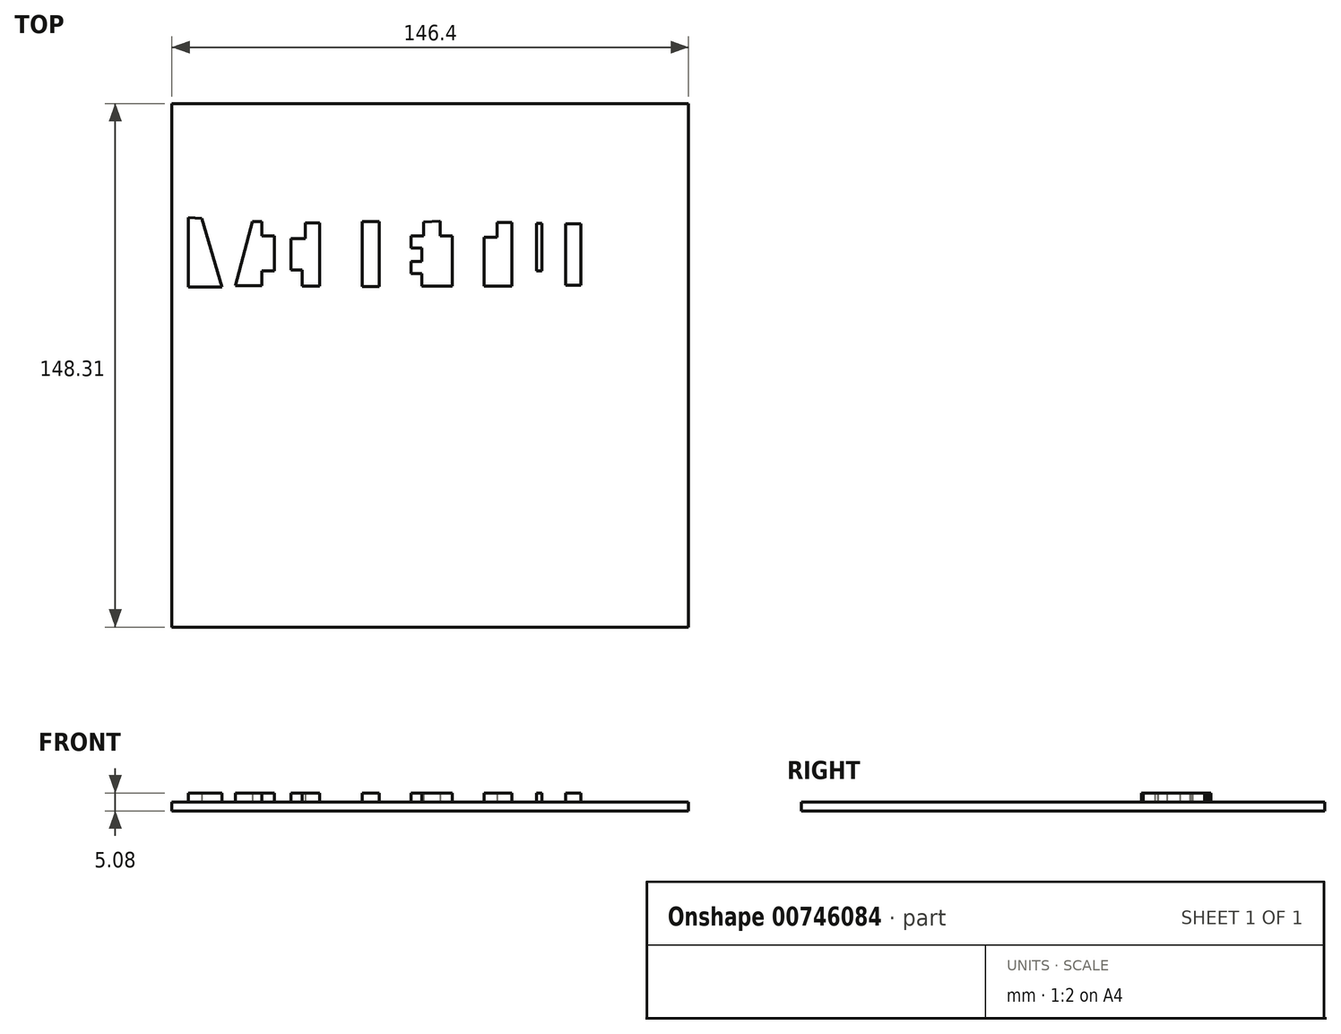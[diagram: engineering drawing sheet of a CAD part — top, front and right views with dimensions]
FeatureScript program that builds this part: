
annotation { "Feature Type Name" : "Feature", "Feature Type Description" : "" }
export const myFeature = defineFeature(function(context is Context, id is Id, definition is map)
    precondition{}
    {
        {
            var Q0;
            Q0=qCreatedBy(makeId("Top.planeOp"),FACE);
            var sketch = newSketch(context, id + "F0", { "sketchPlane" : qUnion([Q0])});
            skLineSegment(sketch, "E0.bottom", {"start": v(-73.41, 74.3) * mm, "end": v(72.99, 74.3) * mm});
            skLineSegment(sketch, "E0.top", {"start": v(-73.41, -74.02) * mm, "end": v(72.99, -74.02) * mm});
            skLineSegment(sketch, "E0.left", {"start": v(-73.41, 74.3) * mm, "end": v(-73.41, -74.02) * mm});
            skLineSegment(sketch, "E0.right", {"start": v(72.99, 74.3) * mm, "end": v(72.99, -74.02) * mm});
            skSolve(sketch);
        }
        {
            var Q0;
            Q0=makeQuery(id+"F0.imprint","IMPRINT",FACE,{"disambiguationData":[TD([[makeQuery(id+"F0.imprint","IMPRINT",EDGE,{"derivedFrom":sQuery(id+"F0.wireOp",EDGE,"E0.bottom")}),-1.0]])]});
            extrude(context, id + "F1", {"entities" : qUnion([Q0]), "depth" : 2.54 * mm, "offsetDistance" : 25.4 * mm});
        }
        {
            var Q0;
            Q0=qCreatedBy(makeId("Top.planeOp"),FACE);
            cPlane(context, id + "F2", {"entities" : qUnion([Q0]), "cplaneType" : CPlaneType.OFFSET, "offset" : 2.54 * mm, "width" : 152.4 * mm, "height" : 152.4 * mm});
        }
        {
            var Q0;
            Q0=qCreatedBy(id+"F2.planeOp",FACE);
            var sketch = newSketch(context, id + "F3", { "sketchPlane" : qUnion([Q0])});
            skLineSegment(sketch, "E1", {"start": v(-68.7, 42.02) * mm, "end": v(-68.7, 22.38) * mm});
            skLineSegment(sketch, "E2", {"start": v(-68.7, 22.38) * mm, "end": v(-59.25, 22.38) * mm});
            skLineSegment(sketch, "E3", {"start": v(-59.25, 22.38) * mm, "end": v(-64.96, 41.77) * mm});
            skLineSegment(sketch, "E4", {"start": v(-64.96, 41.77) * mm, "end": v(-68.7, 42.02) * mm});
            skSolve(sketch);
        }
        {
            var Q0;
            Q0=makeQuery(id+"F3.imprint","IMPRINT",FACE,{"disambiguationData":[TD([[makeQuery(id+"F3.imprint","IMPRINT",EDGE,{"derivedFrom":sQuery(id+"F3.wireOp",EDGE,"E1")}),1.0]])]});
            extrude(context, id + "F4", {"entities" : qUnion([Q0]), "operationType" : NewBodyOperationType.ADD, "depth" : 2.54 * mm, "offsetDistance" : 25.4 * mm});
        }
        {
            var Q0;
            Q0=qCreatedBy(id+"F2.planeOp",FACE);
            var sketch = newSketch(context, id + "F5", { "sketchPlane" : qUnion([Q0])});
            skLineSegment(sketch, "E5", {"start": v(-55.37, 22.74) * mm, "end": v(-47.92, 22.74) * mm});
            skLineSegment(sketch, "E6", {"start": v(-47.92, 22.74) * mm, "end": v(-47.92, 26.92) * mm});
            skLineSegment(sketch, "E7", {"start": v(-47.92, 26.92) * mm, "end": v(-44.4, 26.92) * mm});
            skLineSegment(sketch, "E8", {"start": v(-44.4, 26.92) * mm, "end": v(-44.4, 36.84) * mm});
            skLineSegment(sketch, "E9", {"start": v(-44.4, 36.84) * mm, "end": v(-47.92, 36.84) * mm});
            skLineSegment(sketch, "E10", {"start": v(-47.92, 36.84) * mm, "end": v(-47.92, 40.86) * mm});
            skLineSegment(sketch, "E11", {"start": v(-47.92, 40.86) * mm, "end": v(-50.53, 40.86) * mm});
            skLineSegment(sketch, "E12", {"start": v(-50.53, 40.86) * mm, "end": v(-55.37, 22.74) * mm});
            skSolve(sketch);
        }
        {
            var Q0;
            Q0=makeQuery(id+"F5.imprint","IMPRINT",FACE,{"disambiguationData":[TD([[makeQuery(id+"F5.imprint","IMPRINT",EDGE,{"derivedFrom":sQuery(id+"F5.wireOp",EDGE,"E5")}),1.0]])]});
            extrude(context, id + "F6", {"entities" : qUnion([Q0]), "operationType" : NewBodyOperationType.ADD, "depth" : 2.54 * mm, "offsetDistance" : 25.4 * mm});
        }
        {
            var Q0;
            Q0=qCreatedBy(id+"F2.planeOp",FACE);
            var sketch = newSketch(context, id + "F7", { "sketchPlane" : qUnion([Q0])});
            skLineSegment(sketch, "E13", {"start": v(-39.62, 36.06) * mm, "end": v(-39.62, 27.12) * mm});
            skLineSegment(sketch, "E14", {"start": v(-39.62, 27.12) * mm, "end": v(-36.45, 27.12) * mm});
            skLineSegment(sketch, "E15", {"start": v(-36.45, 27.12) * mm, "end": v(-36.45, 22.62) * mm});
            skLineSegment(sketch, "E16", {"start": v(-36.45, 22.62) * mm, "end": v(-31.5, 22.62) * mm});
            skLineSegment(sketch, "E17", {"start": v(-31.5, 22.62) * mm, "end": v(-31.5, 40.5) * mm});
            skLineSegment(sketch, "E18", {"start": v(-31.5, 40.5) * mm, "end": v(-35.62, 40.5) * mm});
            skLineSegment(sketch, "E19", {"start": v(-35.62, 40.5) * mm, "end": v(-35.62, 36.04) * mm});
            skLineSegment(sketch, "E20", {"start": v(-35.62, 36.04) * mm, "end": v(-39.62, 36.06) * mm});
            skSolve(sketch);
        }
        {
            var Q0;
            Q0=makeQuery(id+"F7.imprint","IMPRINT",FACE,{"disambiguationData":[TD([[makeQuery(id+"F7.imprint","IMPRINT",EDGE,{"derivedFrom":sQuery(id+"F7.wireOp",EDGE,"E13")}),1.0]])]});
            extrude(context, id + "F8", {"entities" : qUnion([Q0]), "operationType" : NewBodyOperationType.ADD, "depth" : 2.54 * mm, "offsetDistance" : 25.4 * mm});
        }
        {
            var Q0;
            Q0=qCreatedBy(id+"F2.planeOp",FACE);
            var sketch = newSketch(context, id + "F9", { "sketchPlane" : qUnion([Q0])});
            skLineSegment(sketch, "E21.bottom", {"start": v(-19.46, 40.9) * mm, "end": v(-14.6, 40.9) * mm});
            skLineSegment(sketch, "E21.top", {"start": v(-19.46, 22.48) * mm, "end": v(-14.6, 22.48) * mm});
            skLineSegment(sketch, "E21.left", {"start": v(-19.46, 40.9) * mm, "end": v(-19.46, 22.48) * mm});
            skLineSegment(sketch, "E21.right", {"start": v(-14.6, 40.9) * mm, "end": v(-14.6, 22.48) * mm});
            skSolve(sketch);
        }
        {
            var Q0;
            Q0=makeQuery(id+"F9.imprint","IMPRINT",FACE,{"disambiguationData":[TD([[makeQuery(id+"F9.imprint","IMPRINT",EDGE,{"derivedFrom":sQuery(id+"F9.wireOp",EDGE,"E21.bottom")}),-1.0]])]});
            extrude(context, id + "F10", {"entities" : qUnion([Q0]), "operationType" : NewBodyOperationType.ADD, "depth" : 2.54 * mm, "offsetDistance" : 25.4 * mm});
        }
        {
            var Q0;
            Q0=qCreatedBy(id+"F2.planeOp",FACE);
            var sketch = newSketch(context, id + "F11", { "sketchPlane" : qUnion([Q0])});
            skLineSegment(sketch, "E22", {"start": v(-2.06, 40.8) * mm, "end": v(-2.06, 36.81) * mm});
            skLineSegment(sketch, "E23", {"start": v(-2.06, 36.81) * mm, "end": v(-5.57, 36.81) * mm});
            skLineSegment(sketch, "E24", {"start": v(-5.57, 36.81) * mm, "end": v(-5.57, 33.36) * mm});
            skLineSegment(sketch, "E25", {"start": v(-5.57, 33.36) * mm, "end": v(-2.61, 33.36) * mm});
            skLineSegment(sketch, "E26", {"start": v(-2.61, 33.36) * mm, "end": v(-2.61, 29.6) * mm});
            skLineSegment(sketch, "E27", {"start": v(-2.61, 29.6) * mm, "end": v(-5.57, 29.6) * mm});
            skLineSegment(sketch, "E28", {"start": v(-5.57, 29.6) * mm, "end": v(-5.57, 26.15) * mm});
            skLineSegment(sketch, "E29", {"start": v(-5.57, 26.15) * mm, "end": v(-2.61, 26.15) * mm});
            skLineSegment(sketch, "E30", {"start": v(-2.61, 26.15) * mm, "end": v(-2.61, 22.65) * mm});
            skLineSegment(sketch, "E31", {"start": v(-2.61, 22.65) * mm, "end": v(6.02, 22.65) * mm});
            skLineSegment(sketch, "E32", {"start": v(6.02, 22.65) * mm, "end": v(6.02, 36.81) * mm});
            skLineSegment(sketch, "E33", {"start": v(6.02, 36.81) * mm, "end": v(2.64, 36.81) * mm});
            skLineSegment(sketch, "E34", {"start": v(2.64, 36.81) * mm, "end": v(2.64, 41.01) * mm});
            skLineSegment(sketch, "E35", {"start": v(2.64, 41.01) * mm, "end": v(-2.06, 40.8) * mm});
            skSolve(sketch);
        }
        {
            var Q0;
            Q0=makeQuery(id+"F11.imprint","IMPRINT",FACE,{"disambiguationData":[TD([[makeQuery(id+"F11.imprint","IMPRINT",EDGE,{"derivedFrom":sQuery(id+"F11.wireOp",EDGE,"E22")}),1.0]])]});
            extrude(context, id + "F12", {"entities" : qUnion([Q0]), "operationType" : NewBodyOperationType.ADD, "depth" : 2.54 * mm, "offsetDistance" : 25.4 * mm});
        }
        {
            var Q0;
            Q0=qCreatedBy(id+"F2.planeOp",FACE);
            var sketch = newSketch(context, id + "F13", { "sketchPlane" : qUnion([Q0])});
            skLineSegment(sketch, "E36", {"start": v(15.07, 36.45) * mm, "end": v(15.07, 22.54) * mm});
            skLineSegment(sketch, "E37", {"start": v(15.07, 22.54) * mm, "end": v(22.93, 22.54) * mm});
            skLineSegment(sketch, "E38", {"start": v(22.93, 22.54) * mm, "end": v(22.93, 40.63) * mm});
            skLineSegment(sketch, "E39", {"start": v(22.93, 40.63) * mm, "end": v(18.82, 40.63) * mm});
            skLineSegment(sketch, "E40", {"start": v(18.82, 40.63) * mm, "end": v(18.82, 36.45) * mm});
            skLineSegment(sketch, "E41", {"start": v(18.82, 36.45) * mm, "end": v(15.07, 36.45) * mm});
            skSolve(sketch);
        }
        {
            var Q0;
            Q0=makeQuery(id+"F13.imprint","IMPRINT",FACE,{"disambiguationData":[TD([[makeQuery(id+"F13.imprint","IMPRINT",EDGE,{"derivedFrom":sQuery(id+"F13.wireOp",EDGE,"E36")}),1.0]])]});
            extrude(context, id + "F14", {"entities" : qUnion([Q0]), "operationType" : NewBodyOperationType.ADD, "depth" : 2.54 * mm, "offsetDistance" : 25.4 * mm});
        }
        {
            var Q0;
            Q0=qCreatedBy(id+"F2.planeOp",FACE);
            var sketch = newSketch(context, id + "F15", { "sketchPlane" : qUnion([Q0])});
            skLineSegment(sketch, "E42.bottom", {"start": v(31.5, 40.32) * mm, "end": v(29.92, 40.32) * mm});
            skLineSegment(sketch, "E42.top", {"start": v(31.5, 26.91) * mm, "end": v(29.92, 26.91) * mm});
            skLineSegment(sketch, "E42.left", {"start": v(31.5, 40.32) * mm, "end": v(31.5, 26.91) * mm});
            skLineSegment(sketch, "E42.right", {"start": v(29.92, 40.32) * mm, "end": v(29.92, 26.91) * mm});
            skSolve(sketch);
        }
        {
            var Q0;
            Q0=makeQuery(id+"F15.imprint","IMPRINT",FACE,{"disambiguationData":[TD([[makeQuery(id+"F15.imprint","IMPRINT",EDGE,{"derivedFrom":sQuery(id+"F15.wireOp",EDGE,"E42.bottom")}),1.0]])]});
            extrude(context, id + "F16", {"entities" : qUnion([Q0]), "operationType" : NewBodyOperationType.ADD, "depth" : 2.54 * mm, "offsetDistance" : 25.4 * mm});
        }
        {
            var Q0;
            Q0=qCreatedBy(id+"F2.planeOp",FACE);
            var sketch = newSketch(context, id + "F17", { "sketchPlane" : qUnion([Q0])});
            skLineSegment(sketch, "E43.bottom", {"start": v(38.2, 40.28) * mm, "end": v(42.57, 40.28) * mm});
            skLineSegment(sketch, "E43.top", {"start": v(38.2, 22.85) * mm, "end": v(42.57, 22.85) * mm});
            skLineSegment(sketch, "E43.left", {"start": v(38.2, 40.28) * mm, "end": v(38.2, 22.85) * mm});
            skLineSegment(sketch, "E43.right", {"start": v(42.57, 40.28) * mm, "end": v(42.57, 22.85) * mm});
            skSolve(sketch);
        }
        {
            var Q0;
            Q0=makeQuery(id+"F17.imprint","IMPRINT",FACE,{"disambiguationData":[TD([[makeQuery(id+"F17.imprint","IMPRINT",EDGE,{"derivedFrom":sQuery(id+"F17.wireOp",EDGE,"E43.bottom")}),-1.0]])]});
            extrude(context, id + "F18", {"entities" : qUnion([Q0]), "operationType" : NewBodyOperationType.ADD, "depth" : 2.54 * mm, "offsetDistance" : 25.4 * mm});
        }
    });
